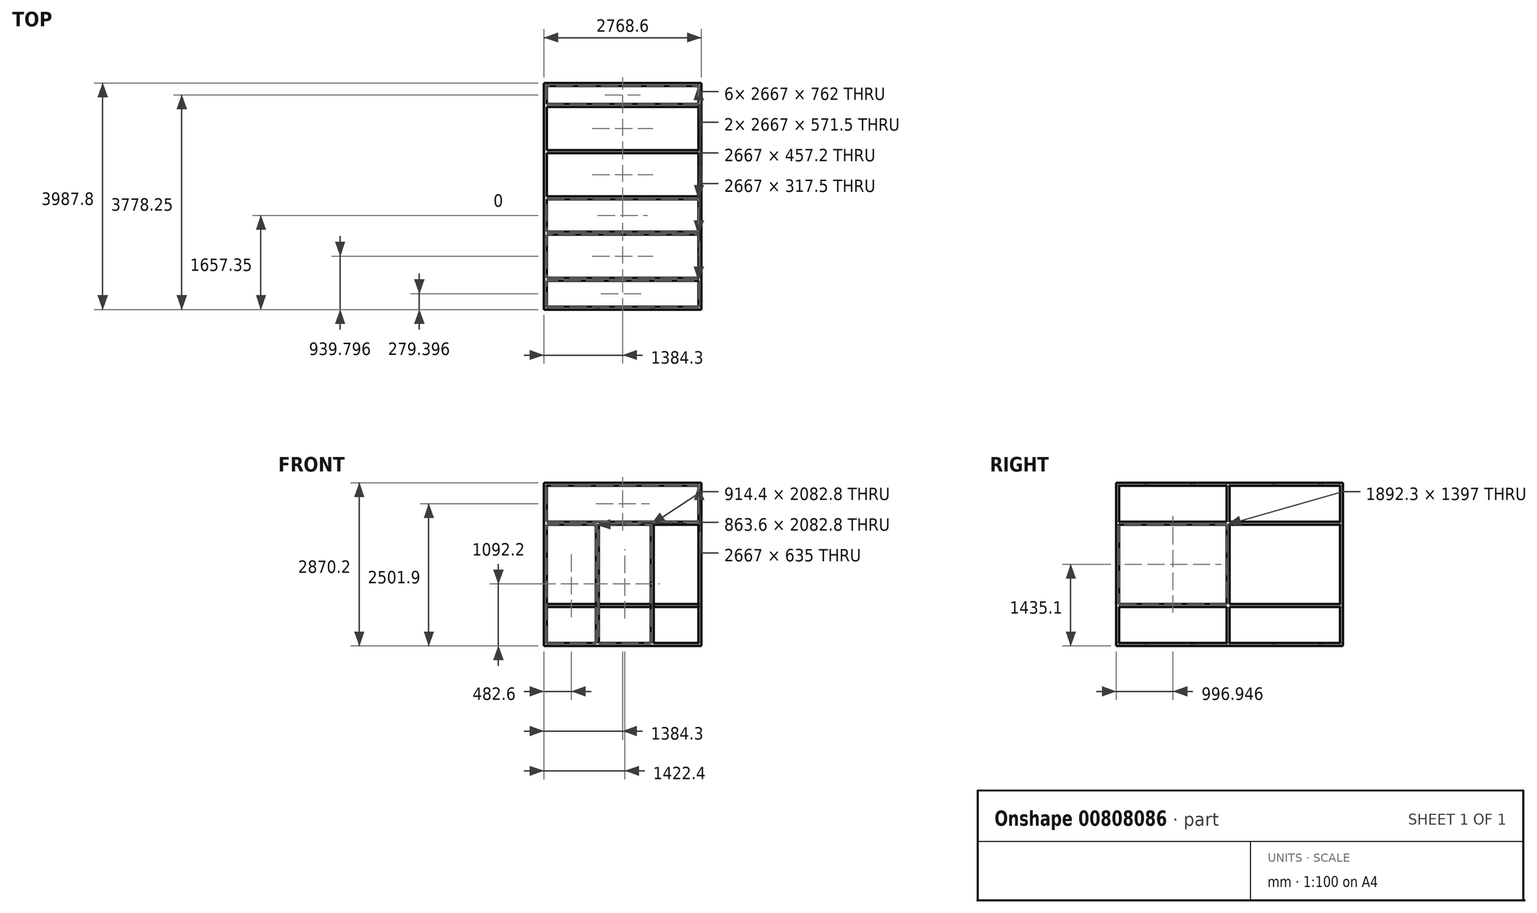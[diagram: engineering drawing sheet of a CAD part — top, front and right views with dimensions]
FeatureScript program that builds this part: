
annotation { "Feature Type Name" : "Feature", "Feature Type Description" : "" }
export const myFeature = defineFeature(function(context is Context, id is Id, definition is map)
    precondition{}
    {
        {
            var Q0;
            Q0=qCreatedBy(makeId("Right.planeOp"),FACE);
            var sketch = newSketch(context, id + "F0", { "sketchPlane" : qUnion([Q0])});
            skLineSegment(sketch, "E0.bottom", {"start": v(-2788.9, 736.6) * mm, "end": v(-2738.1, 736.6) * mm});
            skLineSegment(sketch, "E0.top", {"start": v(-2788.9, -2133.6) * mm, "end": v(-2738.1, -2133.6) * mm});
            skLineSegment(sketch, "E0.left", {"start": v(-2788.9, 736.6) * mm, "end": v(-2788.9, -2133.6) * mm});
            skLineSegment(sketch, "E0.right", {"start": v(-2738.1, 736.6) * mm, "end": v(-2738.1, -2133.6) * mm});
            skLineSegment(sketch, "E1.bottom", {"start": v(-2738.1, 736.6) * mm, "end": v(1148.1, 736.6) * mm});
            skLineSegment(sketch, "E1.top", {"start": v(-2738.1, 685.8) * mm, "end": v(1148.1, 685.8) * mm});
            skLineSegment(sketch, "E1.left", {"start": v(-2738.1, 736.6) * mm, "end": v(-2738.1, 685.8) * mm});
            skLineSegment(sketch, "E1.right", {"start": v(1148.1, 736.6) * mm, "end": v(1148.1, 685.8) * mm});
            skLineSegment(sketch, "E2.bottom", {"start": v(-2738.1, -2082.8) * mm, "end": v(1148.1, -2082.8) * mm});
            skLineSegment(sketch, "E2.top", {"start": v(-2738.1, -2133.6) * mm, "end": v(1148.1, -2133.6) * mm});
            skLineSegment(sketch, "E2.left", {"start": v(-2738.1, -2082.8) * mm, "end": v(-2738.1, -2133.6) * mm});
            skPoint(sketch, "E3.oppositeSnap0", {"position": v(1148.1, -2108.2) * mm});
            skLineSegment(sketch, "E3.bottom", {"start": v(-2738.1, 50.8) * mm, "end": v(1148.1, 50.8) * mm});
            skLineSegment(sketch, "E3.top", {"start": v(-2738.1, 0) * mm, "end": v(1148.1, 0) * mm});
            skLineSegment(sketch, "E3.left", {"start": v(-2738.1, 50.8) * mm, "end": v(-2738.1, 0) * mm});
            skLineSegment(sketch, "E3.right", {"start": v(1148.1, 50.8) * mm, "end": v(1148.1, 0) * mm});
            skLineSegment(sketch, "E4.bottom", {"start": v(1148.1, 736.6) * mm, "end": v(1198.9, 736.6) * mm});
            skLineSegment(sketch, "E4.top", {"start": v(1148.1, -2133.6) * mm, "end": v(1198.9, -2133.6) * mm});
            skLineSegment(sketch, "E4.left", {"start": v(1148.1, 736.6) * mm, "end": v(1148.1, -2082.8) * mm});
            skLineSegment(sketch, "E4.right", {"start": v(1198.9, 736.6) * mm, "end": v(1198.9, -2133.6) * mm});
            skLineSegment(sketch, "E5.bottom", {"start": v(-845.8, 685.8) * mm, "end": v(-795, 685.8) * mm});
            skLineSegment(sketch, "E5.top", {"start": v(-845.8, 50.8) * mm, "end": v(-795, 50.8) * mm});
            skLineSegment(sketch, "E5.left", {"start": v(-845.8, 685.8) * mm, "end": v(-845.8, 50.8) * mm});
            skLineSegment(sketch, "E5.right", {"start": v(-795, 685.8) * mm, "end": v(-795, 50.8) * mm});
            skLineSegment(sketch, "E6.bottom", {"start": v(-845.8, 0) * mm, "end": v(-795, 0) * mm});
            skLineSegment(sketch, "E6.top", {"start": v(-845.8, -2082.8) * mm, "end": v(-795, -2082.8) * mm});
            skLineSegment(sketch, "E6.left", {"start": v(-845.8, 0) * mm, "end": v(-845.8, -1397) * mm});
            skLineSegment(sketch, "E6.right", {"start": v(-795, 0) * mm, "end": v(-795, -1397) * mm});
            skLineSegment(sketch, "E7", {"start": v(1148.1, -2082.8) * mm, "end": v(1148.1, -2133.6) * mm});
            skLineSegment(sketch, "E8.bottom", {"start": v(-2738.1, -1447.8) * mm, "end": v(1148.1, -1447.8) * mm});
            skLineSegment(sketch, "E8.top", {"start": v(-2738.1, -1397) * mm, "end": v(1148.1, -1397) * mm});
            skLineSegment(sketch, "E8.left", {"start": v(-2738.1, -1447.8) * mm, "end": v(-2738.1, -1397) * mm});
            skLineSegment(sketch, "E8.right", {"start": v(1148.1, -1447.8) * mm, "end": v(1148.1, -1397) * mm});
            skLineSegment(sketch, "E9.trimOffspring", {"start": v(-845.8, -1447.8) * mm, "end": v(-845.8, -2082.8) * mm});
            skLineSegment(sketch, "E10.trimOffspring", {"start": v(-795, -1447.8) * mm, "end": v(-795, -2082.8) * mm});
            skSolve(sketch);
        }
        {
            var Q0;
            Q0=qSketchRegion(id+"F0",true);
            var Q1;
            {var subQ5=sQuery(id+"F0.wireOp",EDGE,"E3.left");Q1=makeQuery(id+"F0.imprint","IMPRINT",FACE,{"disambiguationData":[TD([[makeQuery(id+"F0.imprint","IMPRINT",EDGE,{"derivedFrom":subQ5}),1.0]])]});}
            var Q2;
            Q2=makeQuery(id+"F0.imprint","IMPRINT",FACE,{"disambiguationData":[TD([[makeQuery(id+"F0.imprint","IMPRINT",EDGE,{"derivedFrom":sQuery(id+"F0.wireOp",EDGE,"E5.bottom")}),-1.0]])]});
            var Q3;
            Q3=makeQuery(id+"F0.imprint","IMPRINT",FACE,{"disambiguationData":[TD([[makeQuery(id+"F0.imprint","IMPRINT",EDGE,{"derivedFrom":sQuery(id+"F0.wireOp",EDGE,"E6.bottom")}),-1.0]])]});
            var Q4;
            Q4=makeQuery(id+"F0.imprint","IMPRINT",FACE,{"disambiguationData":[TD([[makeQuery(id+"F0.imprint","IMPRINT",EDGE,{"derivedFrom":sQuery(id+"F0.wireOp",EDGE,"E6.top")}),1.0]])]});
            var Q5;
            {var subQ2=sQuery(id+"F0.wireOp",EDGE,"E8.left");Q5=makeQuery(id+"F0.imprint","IMPRINT",FACE,{"disambiguationData":[TD([[makeQuery(id+"F0.imprint","IMPRINT",EDGE,{"derivedFrom":subQ2}),-1.0]])]});}
            extrude(context, id + "F1", {"entities" : qUnion([Q0, Q1, Q2, Q3, Q4, Q5]), "depth" : 50.8 * mm});
        }
        {
            var Q0;
            Q0=makeQuery(id+"F1.opExtrude","CAP_FACE",FACE,{"disambiguationData":[OSD([sQuery(id+"F0.wireOp",EDGE,"E0.bottom"),sQuery(id+"F0.wireOp",EDGE,"E0.top"),sQuery(id+"F0.wireOp",EDGE,"E0.left"),sQuery(id+"F0.wireOp",EDGE,"E0.right"),sQuery(id+"F0.wireOp",EDGE,"E1.bottom"),sQuery(id+"F0.wireOp",EDGE,"E1.top"),sQuery(id+"F0.wireOp",EDGE,"E2.bottom"),sQuery(id+"F0.wireOp",EDGE,"E2.top"),sQuery(id+"F0.wireOp",EDGE,"E3.bottom"),sQuery(id+"F0.wireOp",EDGE,"E3.top"),sQuery(id+"F0.wireOp",EDGE,"E4.bottom"),sQuery(id+"F0.wireOp",EDGE,"E4.top"),sQuery(id+"F0.wireOp",EDGE,"E4.left"),sQuery(id+"F0.wireOp",EDGE,"E4.right"),sQuery(id+"F0.wireOp",EDGE,"E5.left"),sQuery(id+"F0.wireOp",EDGE,"E5.right"),sQuery(id+"F0.wireOp",EDGE,"E6.left"),sQuery(id+"F0.wireOp",EDGE,"E6.right"),sQuery(id+"F0.wireOp",EDGE,"E8.bottom"),sQuery(id+"F0.wireOp",EDGE,"E8.top"),sQuery(id+"F0.wireOp",EDGE,"E9.trimOffspring"),sQuery(id+"F0.wireOp",EDGE,"E10.trimOffspring")])],"isStart":false});
            var sketch = newSketch(context, id + "F2", { "sketchPlane" : qUnion([Q0])});
            skLineSegment(sketch, "E11.bottom", {"start": v(-2738.1, 685.8) * mm, "end": v(-2788.9, 685.8) * mm});
            skLineSegment(sketch, "E11.top", {"start": v(-2738.1, 736.6) * mm, "end": v(-2788.9, 736.6) * mm});
            skLineSegment(sketch, "E11.left", {"start": v(-2738.1, 685.8) * mm, "end": v(-2738.1, 736.6) * mm});
            skLineSegment(sketch, "E11.right", {"start": v(-2788.9, 685.8) * mm, "end": v(-2788.9, 736.6) * mm});
            skLineSegment(sketch, "E12.bottom", {"start": v(-2738.1, 0) * mm, "end": v(-2788.9, 0) * mm});
            skLineSegment(sketch, "E12.top", {"start": v(-2738.1, 50.8) * mm, "end": v(-2788.9, 50.8) * mm});
            skLineSegment(sketch, "E12.left", {"start": v(-2738.1, 0) * mm, "end": v(-2738.1, 50.8) * mm});
            skLineSegment(sketch, "E12.right", {"start": v(-2788.9, 0) * mm, "end": v(-2788.9, 50.8) * mm});
            skLineSegment(sketch, "E13.bottom", {"start": v(-2788.9, -2133.6) * mm, "end": v(-2738.1, -2133.6) * mm});
            skLineSegment(sketch, "E13.top", {"start": v(-2788.9, -2082.8) * mm, "end": v(-2738.1, -2082.8) * mm});
            skLineSegment(sketch, "E13.left", {"start": v(-2788.9, -2133.6) * mm, "end": v(-2788.9, -2082.8) * mm});
            skLineSegment(sketch, "E13.right", {"start": v(-2738.1, -2133.6) * mm, "end": v(-2738.1, -2082.8) * mm});
            skLineSegment(sketch, "E14.bottom", {"start": v(-845.8, -2082.8) * mm, "end": v(-795, -2082.8) * mm});
            skLineSegment(sketch, "E14.top", {"start": v(-845.8, -2133.6) * mm, "end": v(-795, -2133.6) * mm});
            skLineSegment(sketch, "E14.left", {"start": v(-845.8, -2082.8) * mm, "end": v(-845.8, -2133.6) * mm});
            skLineSegment(sketch, "E14.right", {"start": v(-795, -2082.8) * mm, "end": v(-795, -2133.6) * mm});
            skLineSegment(sketch, "E15.bottom", {"start": v(1148.1, -2082.8) * mm, "end": v(1198.9, -2082.8) * mm});
            skLineSegment(sketch, "E15.top", {"start": v(1148.1, -2133.6) * mm, "end": v(1198.9, -2133.6) * mm});
            skLineSegment(sketch, "E15.left", {"start": v(1148.1, -2082.8) * mm, "end": v(1148.1, -2133.6) * mm});
            skLineSegment(sketch, "E15.right", {"start": v(1198.9, -2082.8) * mm, "end": v(1198.9, -2133.6) * mm});
            skLineSegment(sketch, "E16.bottom", {"start": v(1148.1, -1397) * mm, "end": v(1198.9, -1397) * mm});
            skLineSegment(sketch, "E16.top", {"start": v(1148.1, -1447.8) * mm, "end": v(1198.9, -1447.8) * mm});
            skLineSegment(sketch, "E16.left", {"start": v(1148.1, -1397) * mm, "end": v(1148.1, -1447.8) * mm});
            skLineSegment(sketch, "E16.right", {"start": v(1198.9, -1397) * mm, "end": v(1198.9, -1447.8) * mm});
            skLineSegment(sketch, "E17.bottom", {"start": v(1148.1, 50.8) * mm, "end": v(1198.9, 50.8) * mm});
            skLineSegment(sketch, "E17.top", {"start": v(1148.1, 0) * mm, "end": v(1198.9, 0) * mm});
            skLineSegment(sketch, "E17.left", {"start": v(1148.1, 50.8) * mm, "end": v(1148.1, 0) * mm});
            skLineSegment(sketch, "E17.right", {"start": v(1198.9, 50.8) * mm, "end": v(1198.9, 0) * mm});
            skLineSegment(sketch, "E18.bottom", {"start": v(1148.1, 685.8) * mm, "end": v(1198.9, 685.8) * mm});
            skLineSegment(sketch, "E18.top", {"start": v(1148.1, 736.6) * mm, "end": v(1198.9, 736.6) * mm});
            skLineSegment(sketch, "E18.left", {"start": v(1148.1, 685.8) * mm, "end": v(1148.1, 736.6) * mm});
            skLineSegment(sketch, "E18.right", {"start": v(1198.9, 685.8) * mm, "end": v(1198.9, 736.6) * mm});
            skLineSegment(sketch, "E19.bottom", {"start": v(-845.8, 685.8) * mm, "end": v(-795, 685.8) * mm});
            skLineSegment(sketch, "E19.top", {"start": v(-845.8, 736.6) * mm, "end": v(-795, 736.6) * mm});
            skLineSegment(sketch, "E19.left", {"start": v(-845.8, 685.8) * mm, "end": v(-845.8, 736.6) * mm});
            skLineSegment(sketch, "E19.right", {"start": v(-795, 685.8) * mm, "end": v(-795, 736.6) * mm});
            skLineSegment(sketch, "E20.bottom", {"start": v(-2280.9, -2082.8) * mm, "end": v(-2230.1, -2082.8) * mm});
            skLineSegment(sketch, "E20.top", {"start": v(-2280.9, -2133.6) * mm, "end": v(-2230.1, -2133.6) * mm});
            skLineSegment(sketch, "E20.left", {"start": v(-2230.1, -2082.8) * mm, "end": v(-2230.1, -2133.6) * mm});
            skLineSegment(sketch, "E20.right", {"start": v(-2280.9, -2082.8) * mm, "end": v(-2280.9, -2133.6) * mm});
            skLineSegment(sketch, "E21.bottom", {"start": v(-1468.1, -2082.8) * mm, "end": v(-1417.3, -2082.8) * mm});
            skLineSegment(sketch, "E21.top", {"start": v(-1468.1, -2133.6) * mm, "end": v(-1417.3, -2133.6) * mm});
            skLineSegment(sketch, "E21.left", {"start": v(-1417.3, -2082.8) * mm, "end": v(-1417.3, -2133.6) * mm});
            skLineSegment(sketch, "E21.right", {"start": v(-1468.1, -2082.8) * mm, "end": v(-1468.1, -2133.6) * mm});
            skLineSegment(sketch, "E22.bottom", {"start": v(-33, -2082.8) * mm, "end": v(17.8, -2082.8) * mm});
            skLineSegment(sketch, "E22.top", {"start": v(-33, -2133.6) * mm, "end": v(17.8, -2133.6) * mm});
            skLineSegment(sketch, "E22.left", {"start": v(17.8, -2082.8) * mm, "end": v(17.8, -2133.6) * mm});
            skLineSegment(sketch, "E22.right", {"start": v(-33, -2082.8) * mm, "end": v(-33, -2133.6) * mm});
            skLineSegment(sketch, "E23.bottom", {"start": v(779.8, -2082.8) * mm, "end": v(830.6, -2082.8) * mm});
            skLineSegment(sketch, "E23.top", {"start": v(779.8, -2133.6) * mm, "end": v(830.6, -2133.6) * mm});
            skLineSegment(sketch, "E23.left", {"start": v(830.6, -2082.8) * mm, "end": v(830.6, -2133.6) * mm});
            skLineSegment(sketch, "E23.right", {"start": v(779.8, -2082.8) * mm, "end": v(779.8, -2133.6) * mm});
            skLineSegment(sketch, "E24.bottom", {"start": v(779.8, 736.6) * mm, "end": v(830.6, 736.6) * mm});
            skLineSegment(sketch, "E24.top", {"start": v(779.8, 685.8) * mm, "end": v(830.6, 685.8) * mm});
            skLineSegment(sketch, "E24.left", {"start": v(779.8, 736.6) * mm, "end": v(779.8, 685.8) * mm});
            skLineSegment(sketch, "E24.right", {"start": v(830.6, 736.6) * mm, "end": v(830.6, 685.8) * mm});
            skLineSegment(sketch, "E25.bottom", {"start": v(-33, 736.6) * mm, "end": v(17.8, 736.6) * mm});
            skLineSegment(sketch, "E25.top", {"start": v(-33, 685.8) * mm, "end": v(17.8, 685.8) * mm});
            skLineSegment(sketch, "E25.left", {"start": v(-33, 736.6) * mm, "end": v(-33, 685.8) * mm});
            skLineSegment(sketch, "E25.right", {"start": v(17.8, 736.6) * mm, "end": v(17.8, 685.8) * mm});
            skLineSegment(sketch, "E26.bottom", {"start": v(-1468.1, 736.6) * mm, "end": v(-1417.3, 736.6) * mm});
            skLineSegment(sketch, "E26.top", {"start": v(-1468.1, 685.8) * mm, "end": v(-1417.3, 685.8) * mm});
            skLineSegment(sketch, "E26.left", {"start": v(-1468.1, 736.6) * mm, "end": v(-1468.1, 685.8) * mm});
            skLineSegment(sketch, "E26.right", {"start": v(-1417.3, 736.6) * mm, "end": v(-1417.3, 685.8) * mm});
            skLineSegment(sketch, "E27.bottom", {"start": v(-2280.9, 736.6) * mm, "end": v(-2230.1, 736.6) * mm});
            skLineSegment(sketch, "E27.top", {"start": v(-2280.9, 685.8) * mm, "end": v(-2230.1, 685.8) * mm});
            skLineSegment(sketch, "E27.left", {"start": v(-2280.9, 736.6) * mm, "end": v(-2280.9, 685.8) * mm});
            skLineSegment(sketch, "E27.right", {"start": v(-2230.1, 736.6) * mm, "end": v(-2230.1, 685.8) * mm});
            skSolve(sketch);
        }
        {
            var Q0;
            Q0=qSketchRegion(id+"F2",true);
            extrude(context, id + "F3", {"entities" : qUnion([Q0]), "operationType" : NewBodyOperationType.ADD, "depth" : 2667 * mm, "offsetDistance" : 25.4 * mm});
        }
        {
            var Q0;
            Q0=makeQuery(id+"FdNDkVUfc3hBzRG_1.boolean.opBoolean","MERGE",FACE,{"derivedFrom":[makeQuery(id+"F3.boolean.opBoolean","MERGE",FACE,{"derivedFrom":[makeQuery(id+"F1.opExtrude","SWEPT_FACE",FACE,{"disambiguationData":[OSD([sQuery(id+"F0.wireOp",EDGE,"E0.left")])]}),makeQuery(id+"F3.opExtrude","SWEPT_FACE",FACE,{"disambiguationData":[OSD([sQuery(id+"F2.wireOp",EDGE,"E11.right")])]}),makeQuery(id+"F3.opExtrude","SWEPT_FACE",FACE,{"disambiguationData":[OSD([sQuery(id+"F2.wireOp",EDGE,"E12.right")])]}),makeQuery(id+"F3.opExtrude","SWEPT_FACE",FACE,{"disambiguationData":[OSD([sQuery(id+"F2.wireOp",EDGE,"E13.left")])]})]}),makeQuery(id+"FdNDkVUfc3hBzRG_1.opExtrude","SWEPT_FACE",FACE,{"disambiguationData":[OSD([sQuery(id+"FfMQoUBlJK3mjdx_1.wireOp",EDGE,"7a08f9c4-ca3e-4c06-8aa5-ea3d9b3370a6.left")])]})]});
            var sketch = newSketch(context, id + "F4", { "sketchPlane" : qUnion([Q0])});
            skLineSegment(sketch, "E28.bottom", {"start": v(914.4, 0) * mm, "end": v(965.2, 0) * mm});
            skLineSegment(sketch, "E28.top", {"start": v(914.4, -2082.8) * mm, "end": v(965.2, -2082.8) * mm});
            skLineSegment(sketch, "E28.left", {"start": v(914.4, 0) * mm, "end": v(914.4, -2082.8) * mm});
            skLineSegment(sketch, "E28.right", {"start": v(965.2, 0) * mm, "end": v(965.2, -2082.8) * mm});
            skLineSegment(sketch, "E29.bottom", {"start": v(1879.6, 0) * mm, "end": v(1930.4, 0) * mm});
            skLineSegment(sketch, "E29.top", {"start": v(1879.6, -2082.8) * mm, "end": v(1930.4, -2082.8) * mm});
            skLineSegment(sketch, "E29.left", {"start": v(1879.6, 0) * mm, "end": v(1879.6, -2082.8) * mm});
            skLineSegment(sketch, "E29.right", {"start": v(1930.4, 0) * mm, "end": v(1930.4, -2082.8) * mm});
            skSolve(sketch);
        }
        {
            var Q0;
            Q0=qSketchRegion(id+"F4",true);
            extrude(context, id + "F5", {"entities" : qUnion([Q0]), "operationType" : NewBodyOperationType.ADD, "oppositeDirection" : true, "depth" : 50.8 * mm});
        }
        {
            var Q0;
            Q0=makeQuery(id+"F3.opExtrude","CAP_FACE",FACE,{"disambiguationData":[OSD([sQuery(id+"F2.wireOp",EDGE,"E11.bottom"),sQuery(id+"F2.wireOp",EDGE,"E11.top"),sQuery(id+"F2.wireOp",EDGE,"E11.left"),sQuery(id+"F2.wireOp",EDGE,"E11.right")])],"isStart":false});
            var sketch = newSketch(context, id + "F6", { "sketchPlane" : qUnion([Q0])});
            skLineSegment(sketch, "E30.0", {"start": v(-2788.9, 736.6) * mm, "end": v(1198.9, 736.6) * mm});
            skLineSegment(sketch, "E31.0", {"start": v(-2738.1, 685.8) * mm, "end": v(-845.8, 685.8) * mm});
            skLineSegment(sketch, "E32.0", {"start": v(-2788.9, 736.6) * mm, "end": v(-2788.9, -2133.6) * mm});
            skLineSegment(sketch, "E33.0", {"start": v(-2738.1, 685.8) * mm, "end": v(-2738.1, 50.8) * mm});
            skLineSegment(sketch, "E34.0", {"start": v(-2738.1, 50.8) * mm, "end": v(-845.8, 50.8) * mm});
            skLineSegment(sketch, "E35.0", {"start": v(-2738.1, 0) * mm, "end": v(-845.8, 0) * mm});
            skLineSegment(sketch, "E36.0", {"start": v(-2738.1, 0) * mm, "end": v(-2738.1, -1397) * mm});
            skLineSegment(sketch, "E37.0", {"start": v(-845.8, 685.8) * mm, "end": v(-845.8, 50.8) * mm});
            skLineSegment(sketch, "E38.0", {"start": v(-795, 685.8) * mm, "end": v(-795, 50.8) * mm});
            skLineSegment(sketch, "E39.0", {"start": v(-795, 685.8) * mm, "end": v(1148.1, 685.8) * mm});
            skLineSegment(sketch, "E40.0", {"start": v(1148.1, 685.8) * mm, "end": v(1148.1, 50.8) * mm});
            skLineSegment(sketch, "E41.0", {"start": v(1198.9, 736.6) * mm, "end": v(1198.9, -2133.6) * mm});
            skLineSegment(sketch, "E42.0", {"start": v(-795, 50.8) * mm, "end": v(1148.1, 50.8) * mm});
            skLineSegment(sketch, "E43.0", {"start": v(-795, 0) * mm, "end": v(1148.1, 0) * mm});
            skLineSegment(sketch, "E44.0", {"start": v(1148.1, 0) * mm, "end": v(1148.1, -1397) * mm});
            skLineSegment(sketch, "E45.0", {"start": v(-845.8, 0) * mm, "end": v(-845.8, -1397) * mm});
            skLineSegment(sketch, "E46.0", {"start": v(1148.1, -1447.8) * mm, "end": v(1148.1, -2082.8) * mm});
            skLineSegment(sketch, "E47.0", {"start": v(-795, -1447.8) * mm, "end": v(1148.1, -1447.8) * mm});
            skLineSegment(sketch, "E48.0", {"start": v(-795, -2082.8) * mm, "end": v(1148.1, -2082.8) * mm});
            skLineSegment(sketch, "E49.0", {"start": v(-2788.9, -2133.6) * mm, "end": v(1198.9, -2133.6) * mm});
            skLineSegment(sketch, "E50.0", {"start": v(-2738.1, -2082.8) * mm, "end": v(-845.8, -2082.8) * mm});
            skLineSegment(sketch, "E51.0", {"start": v(-795, -1447.8) * mm, "end": v(-795, -2082.8) * mm});
            skLineSegment(sketch, "E52.0", {"start": v(-845.8, -1447.8) * mm, "end": v(-845.8, -2082.8) * mm});
            skLineSegment(sketch, "E53.0", {"start": v(-2738.1, -1447.8) * mm, "end": v(-845.8, -1447.8) * mm});
            skLineSegment(sketch, "E54.0", {"start": v(-2738.1, -1397) * mm, "end": v(-845.8, -1397) * mm});
            skLineSegment(sketch, "E55.0", {"start": v(-795, 0) * mm, "end": v(-795, -1397) * mm});
            skLineSegment(sketch, "E56.0", {"start": v(-795, -1397) * mm, "end": v(1148.1, -1397) * mm});
            skLineSegment(sketch, "E57.0", {"start": v(-2738.1, -1447.8) * mm, "end": v(-2738.1, -2082.8) * mm});
            skSolve(sketch);
        }
        {
            var Q0;
            Q0=qSketchRegion(id+"F6",true);
            extrude(context, id + "F7", {"entities" : qUnion([Q0]), "operationType" : NewBodyOperationType.ADD, "depth" : 50.8 * mm, "offsetDistance" : 25.4 * mm});
        }
    });
